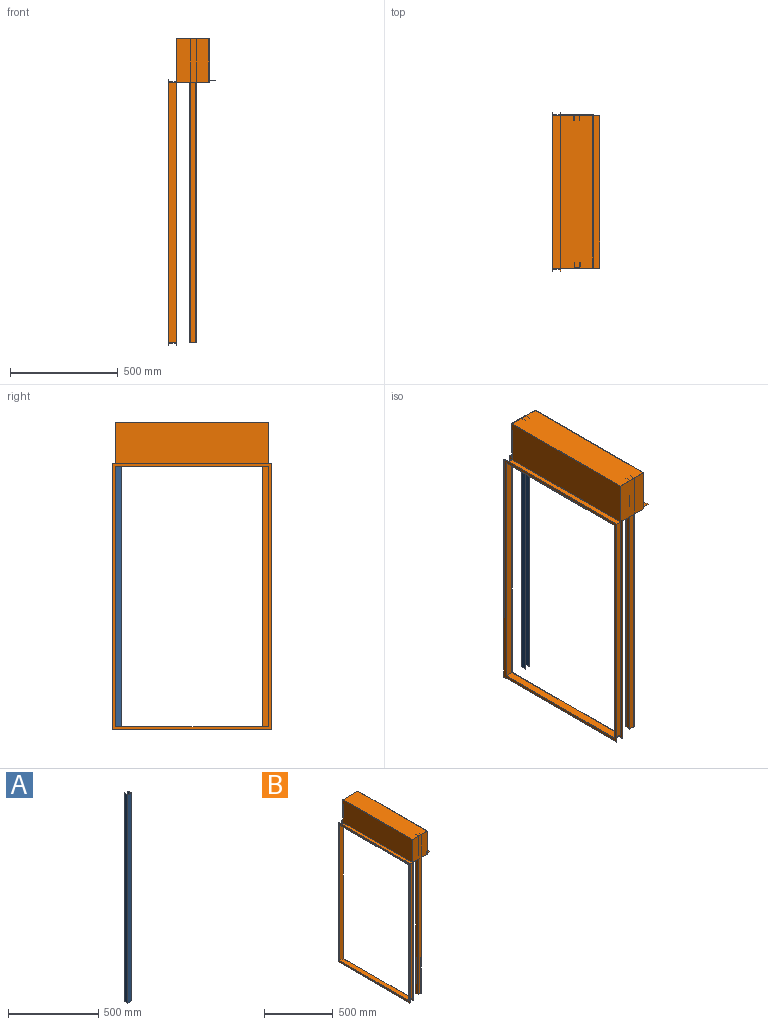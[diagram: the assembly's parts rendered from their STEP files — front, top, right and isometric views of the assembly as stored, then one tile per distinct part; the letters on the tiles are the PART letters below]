
ASSEMBLY  parts=2 mates=1
PART A: 10 faces, bbox 28x26x1414 mm
  f0: plane 1414x24mm, normal (-1,0,0), area 33936mm2, adj f1,f7,f8,f9
  f1: plane 1414x24mm, normal (0,1,0), area 33936mm2, adj f0,f2,f8,f9
  f2: plane 1414x24mm, normal (1,0,0), area 33936mm2, adj f1,f3,f8,f9
  f3: plane 1414x2mm, normal (0,1,0), area 2828mm2, adj f2,f4,f8,f9
  f4: plane 1414x26mm, normal (-1,0,0), area 36764mm2, adj f3,f5,f8,f9
  f5: plane 1414x28mm, normal (0,-1,0), area 39592mm2, adj f4,f6,f8,f9
  f6: plane 1414x26mm, normal (1,0,0), area 36764mm2, adj f5,f7,f8,f9
  f7: plane 1414x2mm, normal (0,1,0), area 2828mm2, adj f0,f6,f8,f9
  f8: plane 28x26mm, normal (0,0,-1), area 152mm2, adj f0,f1,f2,f3,f4,f5,f6,f7
  f9: plane 28x26mm, normal (0,0,1), area 152mm2, adj f0,f1,f2,f3,f4,f5,f6,f7
PART B: 46 faces, bbox 222x740x1431 mm
  f0: plane 710x204mm, normal (1,0,0), area 144840mm2, adj f10,f12,f43,f44
  f1: plane 30x2mm, normal (0,-1,0), area 60mm2, adj f4,f5,f6,f7
  f2: plane 710x204mm, normal (-1,0,0), area 144840mm2, adj f3,f12,f41,f44
  f3: plane 714x152mm, normal (0,0,-1), area 2028mm2, adj f2,f7,f11,f14,f41,f42,f43,f44
  f4: plane 710x30mm, normal (0,0,-1), area 21300mm2, adj f1,f5,f7,f13
  f5: plane 710x2mm, normal (1,0,0), area 1420mm2, adj f1,f4,f6,f13
  f6: plane 710x30mm, normal (0,0,1), area 21300mm2, adj f1,f5,f7,f13
  f7: plane 714x206mm, normal (1,0,0), area 145664mm2, adj f1,f3,f4,f6,f8,f13,f42,f45
  f8: plane 714x154mm, normal (0,0,1), area 109956mm2, adj f7,f9,f42,f45
  f9: plane 1431x740mm, normal (-1,0,0), area 187178mm2, adj f8,f15,f18,f19,f22,f23,f26,f27
  f10: plane 710x40mm, normal (0,0,-1), area 28400mm2, adj f0,f21,f25,f30
  f11: plane 1240x740mm, normal (1,0,0), area 47790mm2, adj f3,f15,f17,f18,f21,f22,f25,f26
  f12: plane 710x150mm, normal (0,0,-1), area 106348mm2, adj f0,f2,f34,f35,f36,f37,f38,f39
  f13: plane 30x2mm, normal (0,1,0), area 60mm2, adj f4,f5,f6,f7
  f14: plane 1210x28mm, normal (0,-1,0), area 33880mm2, adj f3,f33,f34,f39
  f15: plane 13x2mm, normal (0,0,1), area 26mm2, adj f9,f11,f26,f45
  f16: plane 740x2mm, normal (0,0,-1), area 1480mm2, adj f20,f24,f28,f30
  f17: plane 710x40mm, normal (0,0,1), area 28400mm2, adj f11,f21,f25,f30
  f18: plane 740x2mm, normal (0,0,-1), area 1480mm2, adj f9,f11,f22,f26
  f19: plane 714x36mm, normal (0,0,-1), area 25704mm2, adj f9,f23,f27,f28
  f20: plane 1240x2mm, normal (0,-1,0), area 2480mm2, adj f16,f28,f29,f30
  f21: plane 1210x40mm, normal (0,1,0), area 48400mm2, adj f10,f11,f17,f30
  f22: plane 1240x2mm, normal (0,-1,0), area 2480mm2, adj f9,f11,f18,f31
  f23: plane 1214x36mm, normal (0,-1,0), area 43704mm2, adj f9,f19,f28,f32
  f24: plane 1240x2mm, normal (0,1,0), area 2480mm2, adj f16,f28,f29,f30
  f25: plane 1210x40mm, normal (0,-1,0), area 48400mm2, adj f10,f11,f17,f30
  f26: plane 1240x2mm, normal (0,1,0), area 2480mm2, adj f9,f11,f15,f18
  f27: plane 1214x36mm, normal (0,1,0), area 43704mm2, adj f9,f19,f28,f32
  f28: plane 1240x740mm, normal (1,0,0), area 50804mm2, adj f16,f19,f20,f23,f24,f27,f29,f32
  f29: plane 740x2mm, normal (0,0,1), area 1480mm2, adj f20,f24,f28,f30
  f30: plane 1240x740mm, normal (-1,0,0), area 58500mm2, adj f10,f16,f17,f20,f21,f24,f25,f29
  f31: plane 13x2mm, normal (0,0,1), area 26mm2, adj f9,f11,f22,f42
  f32: plane 714x36mm, normal (0,0,1), area 25704mm2, adj f9,f23,f27,f28
  f33: plane 28x26mm, normal (0,0,-1), area 152mm2, adj f14,f34,f35,f36,f37,f38,f39,f40
  f34: plane 1414x26mm, normal (-1,0,0), area 36764mm2, adj f12,f14,f33,f35,f43
  f35: plane 1414x2mm, normal (0,1,0), area 2828mm2, adj f12,f33,f34,f36
  f36: plane 1414x24mm, normal (1,0,0), area 33936mm2, adj f12,f33,f35,f37
  f37: plane 1414x24mm, normal (0,1,0), area 33936mm2, adj f12,f33,f36,f38
  f38: plane 1414x24mm, normal (-1,0,0), area 33936mm2, adj f12,f33,f37,f40
  f39: plane 1414x26mm, normal (1,0,0), area 36764mm2, adj f12,f14,f33,f40,f41
  f40: plane 1414x2mm, normal (0,1,0), area 2828mm2, adj f12,f33,f38,f39
  f41: plane 204x59mm, normal (0,1,0), area 12036mm2, adj f2,f3,f12,f39
  f42: plane 206x154mm, normal (0,-1,0), area 31694mm2, adj f3,f7,f8,f9,f11,f31
  f43: plane 204x63mm, normal (0,1,0), area 12852mm2, adj f0,f3,f12,f34
  f44: plane 204x150mm, normal (0,-1,0), area 30600mm2, adj f0,f2,f3,f12
  f45: plane 206x154mm, normal (0,1,0), area 31694mm2, adj f3,f7,f8,f9,f11,f15
PLACE A rot(axis=(0,0,1),180deg) t=(-407.52,253.41,-201.68)mm
PLACE B t=(-316.52,-456.59,-405.68)mm fixed
MATE planar B.f44 <-> A.f5  axis (0,-1,0) through (-393.52,253.41,-201.68)mm
